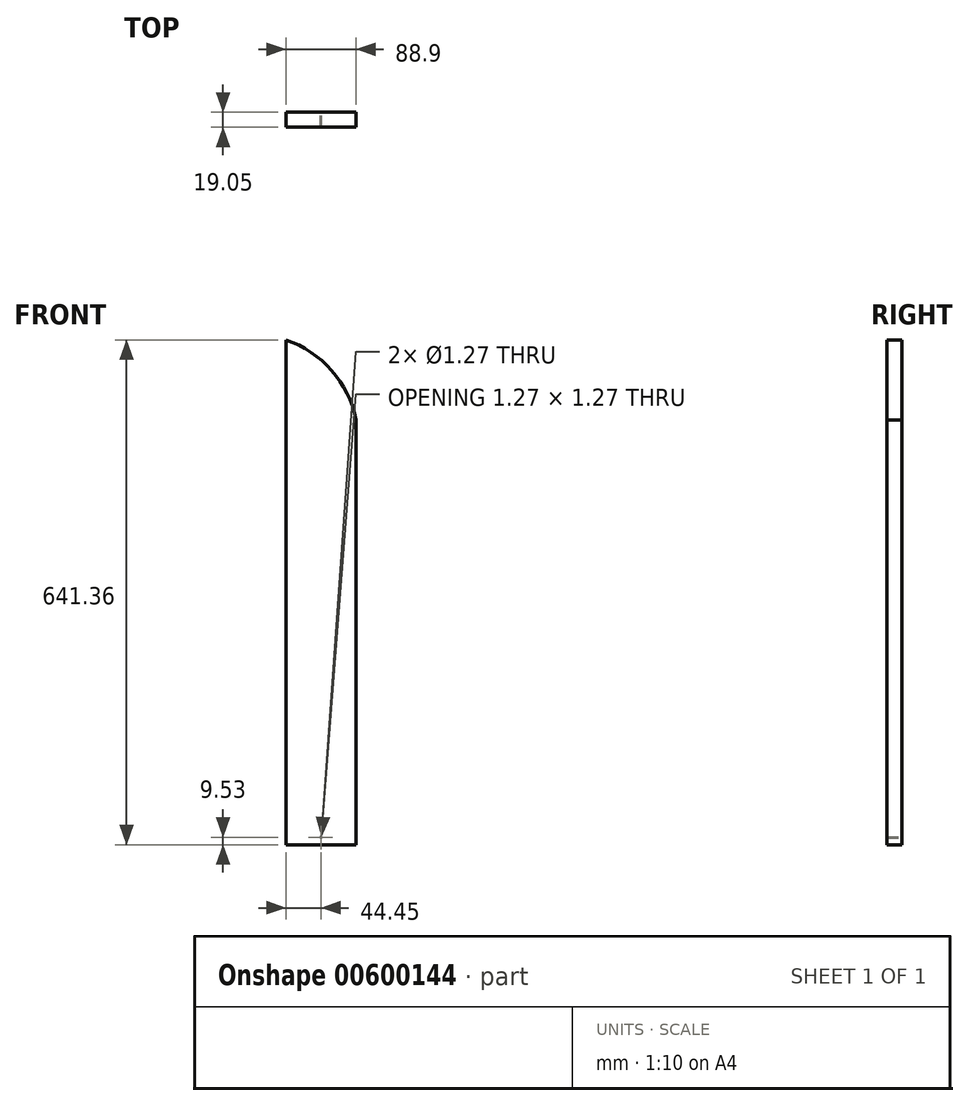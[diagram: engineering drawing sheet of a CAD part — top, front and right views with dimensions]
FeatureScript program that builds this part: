
annotation { "Feature Type Name" : "Feature", "Feature Type Description" : "" }
export const myFeature = defineFeature(function(context is Context, id is Id, definition is map)
    precondition{}
    {
        {
            var Q0;
            Q0=qCreatedBy(makeId("Front.planeOp"),FACE);
            var sketch = newSketch(context, id + "F0", { "sketchPlane" : qUnion([Q0])});
            skLineSegment(sketch, "E0.right", {"start": v(-44.45, 320.68) * mm, "end": v(-44.45, -320.68) * mm});
            skArc(sketch, "E1.MirrorCS", {"start": v(-44.45, 320.68) * mm, "mid": v(13.5, 281.68) * mm, "end": v(44.45, 219.08) * mm});
            skLineSegment(sketch, "E2.MirrorCS", {"start": v(-44.45, 320.68) * mm, "end": v(44.45, -320.68) * mm, "construction": true});
            skLineSegment(sketch, "E3.MirrorCS", {"start": v(44.45, 219.08) * mm, "end": v(44.45, -320.68) * mm});
            skLineSegment(sketch, "E4.MirrorCS", {"start": v(44.45, -320.67) * mm, "end": v(-44.45, -320.68) * mm});
            skSolve(sketch);
        }
        {
            var Q0;
            Q0 = qSketchRegion(id + "F0", true);
            extrude(context, id + "F1", {"entities" : qUnion([Q0]), "depth" : 19.05 * mm, "offsetDistance" : 25.4 * mm});
        }
        {
            var Q0;
            Q0=makeQuery(id+"F1.opExtrude","CAP_FACE",FACE,{"disambiguationData":[OSD([sQuery(id+"F0.wireOp",EDGE,"E0.right"),sQuery(id+"F0.wireOp",EDGE,"E1.MirrorCS"),sQuery(id+"F0.wireOp",EDGE,"E3.MirrorCS"),sQuery(id+"F0.wireOp",EDGE,"E4.MirrorCS")])],"isStart":true});
            var sketch = newSketch(context, id + "F2", { "sketchPlane" : qUnion([Q0])});
            skCircle(sketch, "E5", {"center": v(0, -311.15) * mm, "radius": 0.64 * mm});
            skPoint(sketch, "E5.centerSnap0", {"position": v(0, -320.67) * mm});
            skSolve(sketch);
        }
        {
            var Q0;
            Q0 = qSketchRegion(id + "F2", true);
            extrude(context, id + "F3", {"entities" : qUnion([Q0]), "operationType" : NewBodyOperationType.REMOVE, "endBound" : BoundingType.THROUGH_ALL, "oppositeDirection" : true, "depth" : 25.4 * mm, "offsetDistance" : 25.4 * mm});
        }
    });
